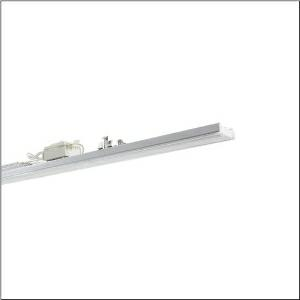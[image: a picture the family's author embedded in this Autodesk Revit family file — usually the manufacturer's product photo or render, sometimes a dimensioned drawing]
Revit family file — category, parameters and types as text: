
# Revit family: licross_r__21_recessed_mo_52tl12dn465g_46f0
name_source: partatom
category: Lighting Fixtures
units: mm (PartAtom-declared; Revit-internal decimal feet)

## family parameters
Cut with Voids When Loaded = No
Host = Face
Light Source = No
Part Type = Normal
Room Calculation Point = No
Round Connector Dimension = Use Diameter
Shared = No

## types (1)
- --- (1 x LED, 6500 lm, 35.1 W, 4000K)
    Apparent Load = 35 VA
    CIE Flux Codes = 72 92 99 100 100
    Color Rendering = 80
    Color Temperature = 4000K
    Default Elevation = 1800 mm
    Description = Licross® 21 Recessed MO, luminaire insert, of sheet steel, galvanised, coil coated, white, length: 1.500mm, width: 66mm, height: 67mm, LED rated luminous flux: 6.500lm, light colour: 840, control gear: DALI 2, with plug, 5-pole, with phase selection, mains connection: 220..240V, AC, 50/60Hz, rated input power: 35W, halogen-free wiring, primary optical cover: cover, of PMMA, light emission: direct distribution, primary light characteristic: symmetric, protection rating (complete): IP40, insulation class (complete): insulation class I (protective earthing), certification: CE, ENEC, VDE, UKCA, protection symbol: D if used in an environment without relevant dust loads with corresponding accessories, impact resistance: IK06, permissible ambient temperature for indoor applications: -25..+45°C, corresponds to IFS (International Featured Standards) requirements for safety and quality in the food industry, reducing of maximum allowable ambient temperature of 5°C with ceiling mounting, LABS conformity tested according to VDMA 24364:2018-05, packaging unit: 1 piece
    Height = 58 mm
    Lamp = 1 x LED
    Lamp Light Flux = 6500 lm
    Lamp Power = 35.1 W
    Lamp count = 1
    Length = 1500 mm
    Luminous efficacy = 185 lm/W
    Manufacturer = Siteco
    ModVariant = No
    Model = 52TL12DN465G
    Mounting Place = Ceiling
    Mounting Type = Pendant
    Number of Poles = 1
    OnlyDefault = Yes
    Power Factor = 1
    Product Name = Licross® 21 Recessed MO
    Product group = luminaire insert
    ProductGroupID = 902
    Protection Class = Protection class I
    Protection Degree = IP 40
    RLX_Detail_Level = 1
    RLX_Emergency_Light_Flux = 0 lm
    RLX_Emergency_Type = 0
    RLX_Emergency_Type_DB = No
    RlxData = <blob elided: 24261 chars, md5=17785872>
    Socket = socket
    Standby Power = 0 W
    System Light Flux = 6500 lm
    System Power = 35 W
    Type Comments = factory setting: luminous flux: 100 % | dim-lin: 254 | 238 mA
    Type Image = l_1296930.jpg
    URL = http://relux.com
    VarID = @adj_126216
    Voltage = 0 V
    Weight = 0.00 kg
    Width = 66 mm

## geometry (parser evidence)
native form markers: Blend x4, Sweep x11
no freeform markers — native parametric forms only
